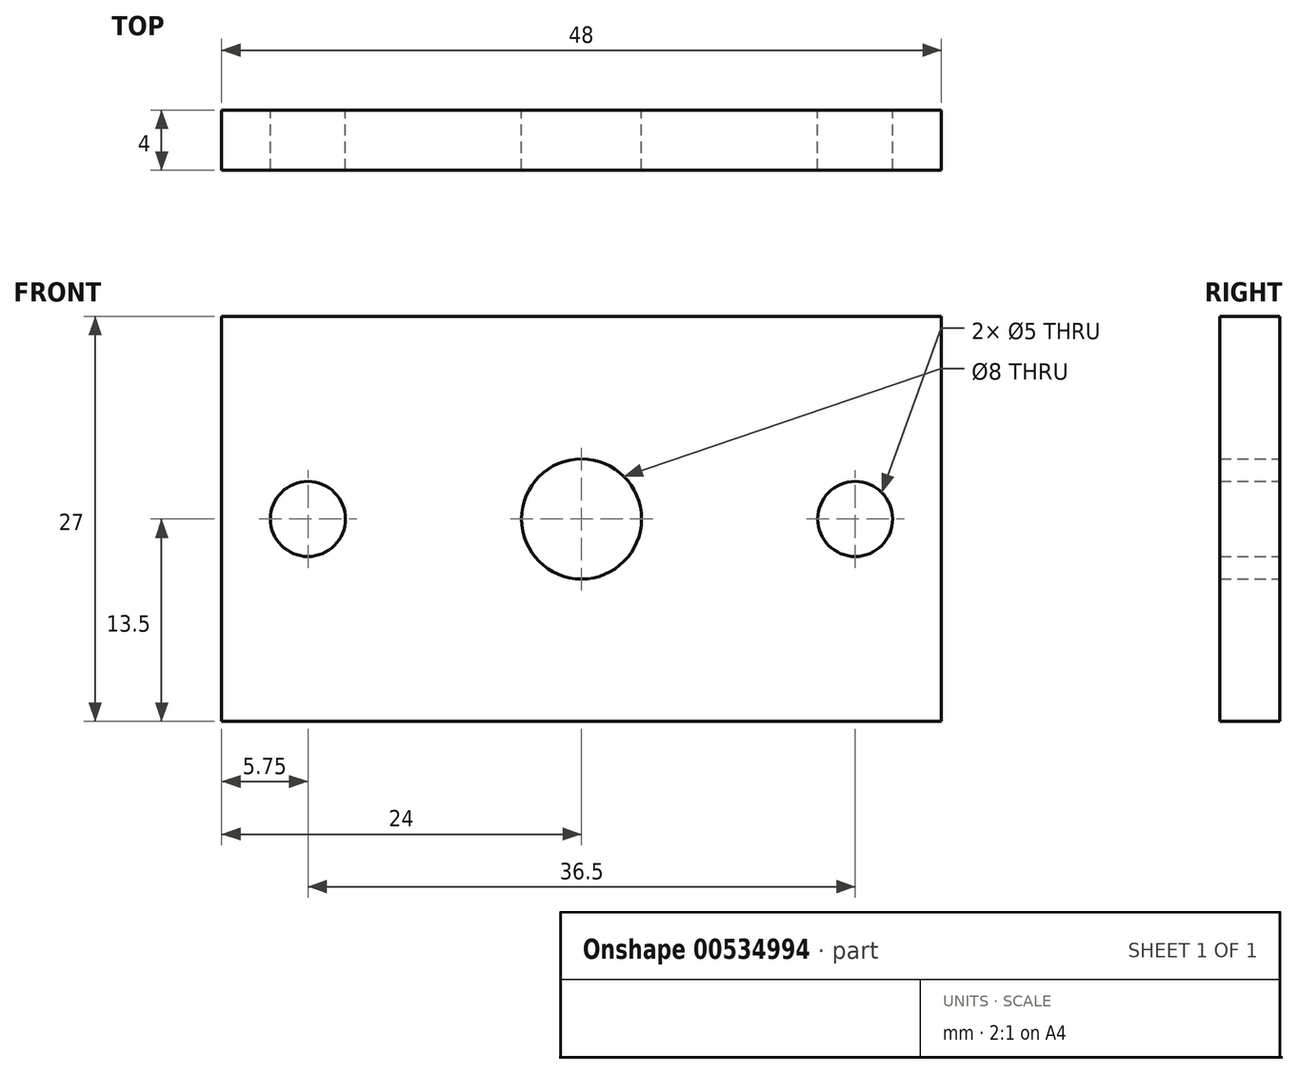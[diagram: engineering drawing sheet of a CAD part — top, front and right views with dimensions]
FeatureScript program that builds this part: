
annotation { "Feature Type Name" : "Feature", "Feature Type Description" : "" }
export const myFeature = defineFeature(function(context is Context, id is Id, definition is map)
    precondition{}
    {
        {
            var Q0;
            Q0=qCreatedBy(makeId("Front.planeOp"),FACE);
            var sketch = newSketch(context, id + "F0", { "sketchPlane" : qUnion([Q0])});
            skCircle(sketch, "E0", {"center": v(0, 0) * mm, "radius": 4 * mm});
            skLineSegment(sketch, "E1", {"start": v(0, 0) * mm, "end": v(24, 0) * mm});
            skLineSegment(sketch, "E2", {"start": v(0, 0) * mm, "end": v(-24, 0) * mm});
            skLineSegment(sketch, "E3", {"start": v(0, 0) * mm, "end": v(0, 13.5) * mm});
            skLineSegment(sketch, "E4", {"start": v(0, 0) * mm, "end": v(0, -13.5) * mm});
            skLineSegment(sketch, "E5", {"start": v(0, 0) * mm, "end": v(18.25, 0) * mm});
            skLineSegment(sketch, "E6", {"start": v(0, 0) * mm, "end": v(-18.25, 0) * mm});
            skCircle(sketch, "E7", {"center": v(-18.25, 0) * mm, "radius": 2.5 * mm});
            skCircle(sketch, "E8", {"center": v(18.25, 0) * mm, "radius": 2.5 * mm});
            skLineSegment(sketch, "E9", {"start": v(0, -13.5) * mm, "end": v(-24, -13.5) * mm});
            skLineSegment(sketch, "E10", {"start": v(-24, -13.5) * mm, "end": v(-24, 0) * mm});
            skLineSegment(sketch, "E11", {"start": v(0, 13.5) * mm, "end": v(-24, 13.5) * mm});
            skLineSegment(sketch, "E12", {"start": v(-24, 0) * mm, "end": v(-24, 13.5) * mm});
            skLineSegment(sketch, "E13", {"start": v(24, 0) * mm, "end": v(24, 13.5) * mm});
            skLineSegment(sketch, "E14", {"start": v(0, 13.5) * mm, "end": v(24, 13.5) * mm});
            skLineSegment(sketch, "E15", {"start": v(24, 0) * mm, "end": v(24, -13.5) * mm});
            skLineSegment(sketch, "E16", {"start": v(0, -13.5) * mm, "end": v(24, -13.5) * mm});
            skSolve(sketch);
        }
        {
            var Q0;
            Q0 = qSketchRegion(id + "F0", true);
            extrude(context, id + "F1", {"entities" : qUnion([Q0]), "depth" : 4 * mm, "offsetDistance" : 25 * mm});
        }
    });
